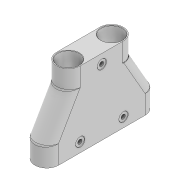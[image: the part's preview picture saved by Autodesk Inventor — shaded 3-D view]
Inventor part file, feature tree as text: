
AUTODESK INVENTOR PART (.ipt)
format: ipt  version: 2020 (Build 240168000, 168)  size: 812,544 bytes
history: native  units: mm
features: sketch x16, fillet x13, projected_geometry x9, sweep x6, extrude x6, plane x2, hole x2, chamfer x2, loft x1
ambient origin geometry x8: Origin, YZ Plane, XZ Plane, XY Plane, X Axis, Y Axis, Z Axis, Center Point
bodies: Solid1 (feature_tree)
feature tree (57):
  sketch  "Sketch1"  dims[d0=22.0mm d1=-40.0mm]
  plane  "Work Plane2"
  loft  "Loft1"
  sketch  "Sketch3"  dims[d10=22.0mm d11=22.0mm]
  sketch  "Sketch4"  dims[d12=22.0mm d13=25.163558mm]
  sweep  "Sweep1"
  sweep  "Sweep2"
  sweep  "Sweep3"
  sweep  "Sweep4"
  sweep  "Sweep5"
  sweep  "Sweep6"
  extrude  "Extrusion1"  Depth=23.0mm
  extrude  "Extrusion2"  Depth=25.2mm
  fillet  "Fillet1"  [1 undecoded]
  fillet  "Fillet2"  [1 undecoded]
  fillet  "Fillet3"  [1 undecoded]
  fillet  "Fillet4"  [1 undecoded]
  fillet  "Fillet5"  Radius=25.0mm
  fillet  "Fillet6"  Radius=30.0mm
  fillet  "Fillet7"  Radius=42.0mm
  fillet  "Fillet8"  Radius=42.0mm
  fillet  "Fillet9"  Radius=42.0mm
  fillet  "Fillet10"  Radius=42.0mm
  fillet  "Fillet11"  Radius=42.0mm
  fillet  "Fillet12"  Radius=42.0mm
  extrude  "Extrusion3"  Depth=42.0mm
  extrude  "Extrusion4"  Depth=42.0mm
  extrude  "Extrusion5"  Depth=42.0mm
  extrude  "Extrusion6"  Depth=42.0mm
  hole  "Hole1"  [1 undecoded]
  hole  "Hole2"  [1 undecoded]
  chamfer  "Chamfer1"  Distance=20.0mm
  chamfer  "Chamfer2"  Distance=20.0mm
  fillet  "Fillet13"  Radius=20.0mm
  plane  "Work Plane1"
  sketch  "Sketch2"  dims[d8=22.0mm d9=22.0mm]
  sketch  "3D Sketch1"
  sketch  "3D Sketch2"
  sketch  "3D Sketch3"
  sketch  "3D Sketch4"
  sketch  "3D Sketch5"
  sketch  "3D Sketch6"
  sketch  "Sketch5"  dims[d14=25.2mm d15=25.2mm]
  projected_geometry  "Projected Loop1"
  sketch  "Sketch7"  dims[d16=0.0mm d17=0.0mm d18=0.0mm d19=0.0mm]
  projected_geometry  "Projected Loop2"
  projected_geometry  "Projected Loop3"
  projected_geometry  "Projected Loop4"
  projected_geometry  "Projected Loop5"
  sketch  "Sketch8"  dims[d20=0.0mm d21=0.0mm d22=0.0mm d23=0.0mm]
  sketch  "Sketch9"  dims[d25=23.0mm d26=23.0mm]
  projected_geometry  "Projected Loop6"
  projected_geometry  "Projected Loop7"
  projected_geometry  "Projected Loop8"
  projected_geometry  "Projected Loop9"
  sketch  "Sketch10"  dims[d27=25.2mm d28=25.2mm d29=0.0mm d30=90.0deg d31=0.0mm d32=90.0deg d33=0.0mm d34=0.0mm d35=0.0mm d36=0.0mm d37=25.0mm d38=0.0mm d39=30.0mm d40=0.0mm d41=42.0mm d42=42.0mm d43=42.0mm d44=42.0mm d45=42.0mm d46=42.0mm]
  sketch  "Sketch11"  dims[d47=42.0mm d48=42.0mm d49=42.0mm d50=42.0mm d51=42.0mm d52=42.0mm d53=20.0mm d54=-0.124791mm d55=20.0mm d56=0.0mm d57=20.0mm d58=-0.124791mm d59=20.0mm d60=0.0mm d61=23.0mm d62=23.0mm d63=0.0mm d64=10.0mm d65=10.0mm d66=10.0mm d67=4.5mm d68=6.0mm d69=7.5mm d70=4.0mm d71=90.0deg d72=8.0mm d73=20.594885mm d74=4.5mm d75=6.0mm d76=10.0mm d77=0.4mm d78=90.0deg d79=8.0mm d80=20.594885mm d81=0.4mm d82=2.0mm d83=45.0deg d84=0.4mm d85=2.0mm d86=45.0deg d87=4.0mm]
note: 6 required parameter values undecoded (feature->parameter linkage not recoverable at this tier; creation-order binding heuristic only, values carry confidence <= 0.55)
